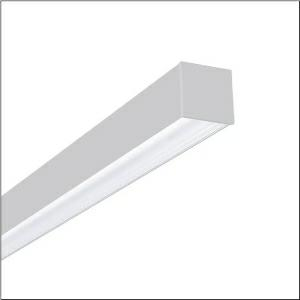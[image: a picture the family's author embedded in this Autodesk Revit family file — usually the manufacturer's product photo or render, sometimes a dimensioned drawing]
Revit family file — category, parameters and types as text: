
# Revit family: silica_r_5mx22wd1w4a_c31c
name_source: partatom
category: Lighting Fixtures
units: mm (PartAtom-declared; Revit-internal decimal feet)

## family parameters
Cut with Voids When Loaded = No
Host = Face
Light Source = No
Part Type = Normal
Room Calculation Point = No
Round Connector Dimension = Use Diameter
Shared = No

## types (1)
- --- (1 x LED, 4680 lm, 29.3 W, 4000K)
    Apparent Load = 29 VA
    CIE Flux Codes = 70 95 99 100 100
    Color Rendering = 80
    Color Temperature = 4000K
    Default Elevation = 1800 mm
    Description = Silica®, office luminaire, primary light control with wallwasher, of aluminium, light emission: direct distribution, primary light characteristic: asymmetric, installation type: surface-mounted, LED rated luminous flux: 4.680 lm, light colour: 840, colour temperature: 4000K, control gear: ECG DALI, with terminal, 3+2-pole, max. 2.5mm², mains connection: 230V, AC, 50/60Hz, rated input power: 29W, luminaire housing, of aluminium, traffic white (RAL 9016), length: 1.440 mm, width: 64 mm, height: 64mm, protection rating (complete): IP20, insulation class (complete): insulation class I (protective earthing), certification: CE, permissible ambient temperature for indoor applications: 0..+35°C, standard: EN 50419, packaging unit: 1 piece
    Height = 64 mm
    Lamp = 1 x LED
    Lamp Light Flux = 4680 lm
    Lamp Power = 29.3 W
    Lamp count = 1
    Length = 1442 mm
    Luminous efficacy = 160 lm/W
    Manufacturer = Siteco
    ModVariant = No
    Model = 5MX22WD1W4A
    Mounting Place = Ceiling
    Mounting Type = Surface mounted
    Number of Poles = 1
    OnlyDefault = Yes
    Power Factor = 1
    Product Name = Silica®
    Product group = office luminaire | ceiling mounted
    ProductGroupID = 302
    Protection Class = Protection class I
    Protection Degree = IP 20
    RLX_Detail_Level = 1
    RlxData = <blob elided: 23977 chars, md5=35fe1cee>
    Socket = socket
    Standby Power = 0 W
    System Light Flux = 4680 lm
    System Power = 29 W
    Type Comments = factory setting: luminous flux: 100 % | dim-lin: 254 | 164 mA
    Type Image = l_1003937.jpg
    URL = http://relux.com
    VarID = @adj_131812
    Voltage = 0 V
    Weight = 0.00 kg
    Width = 66 mm

## geometry (parser evidence)
native form markers: Blend x4, Sweep x11
no freeform markers — native parametric forms only
